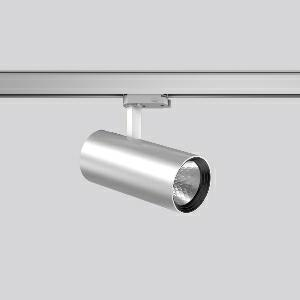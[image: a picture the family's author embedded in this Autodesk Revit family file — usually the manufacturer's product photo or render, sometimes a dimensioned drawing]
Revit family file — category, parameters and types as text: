
# Revit family: deecos_s_mini_742203_004_e2c7
name_source: partatom
category: Lighting Fixtures
units: mm (PartAtom-declared; Revit-internal decimal feet)

## family parameters
Cut with Voids When Loaded = No
Host = Face
Light Source = No
Part Type = Normal
Room Calculation Point = No
Round Connector Dimension = Use Diameter
Shared = No

## types (1)
- DEECOS S mini (1 x LED Modul 930, 3550 lm, 3000)
    Apparent Load = 29 VA
    Approval mark = CE
    CIE Flux Codes = 100 100 100 100 100
    Color Rendering = 90
    Color Temperature = 3000
    Default Elevation = 1800 mm
    Description = Series: DEECOS S mini
LED surface-mounted projector in modern design with no visible cooling ribs. Housing: die-cast aluminium, powder-coated. Rotation range: 356°. Swivel range: 90°. Black plastic ring and recessed LED to prevent glare from the side. Optical assembly with reflector made of MIRO-Silver with 98% total light reflection for outstanding efficiency - can be changed without tools. Best colour rendering index Ra>90. With multi adaptor for 3-circuit tracks 230 V. Suitable for Track on ceiling, Wall track. High quality converter without flickering and stroboscopic effect. The following accessories can be mounted without use of tools: interchangeable lenses, decorative glasses, honeycomb louvre, clear and frosted diffusers, white interchangeable plastic ring. 
Colour: silver
Diameter: 87 mm
Height: 214 mm
Lamp: LED
Socket: without socket
Colour temperature: 3000K
Colour rendering index (CRI): 92
System power: 29 W
Rated luminous flux: 3550 lm
Luminous efficiency: 122 lm/W
Control gear: Regulated power supply
Protection class: I
Type of protection: IP 20
    Height = 214 mm
    Lamp = 1 x LED Modul 930
    Lamp Light Flux = 3550 lm
    Lamp count = 1
    Length = 87 mm
    Lifetime = 50000 h
    Luminous efficacy = 122 lm/W
    Manufacturer = RZB
    ModVariant = No
    Model = 742203.004
    Mounting Place = Ceiling
    Mounting Type = Rail mounted
    Number of Poles = 1
    OnlyDefault = Yes
    Power Factor = 1
    Product Name = DEECOS S mini
    Product group = Track mounted projectors
    ProductGroupID = 301
    Protection Class = Protection class I
    Protection Degree = IP 20
    RLX_Detail_Level = 1
    RLX_Emergency_Light_Flux = 0 lm
    RLX_Emergency_Type = 0
    RLX_Emergency_Type_DB = No
    RlxData = <blob elided: 37021 chars, md5=3e0e8393>
    Socket = socket
    Standby Power = 0 W
    System Light Flux = 3550 lm
    System Power = 29 W
    Type Comments = Product without accessories
    Type Image = 741926.004.jpg
    URL = http://relux.com
    VarID = ---
    Voltage = 230 V
    Voltage Range = 220-240 V
    Weight = 0.00 kg
    Width = 0 mm  [stored 0 ft]

note: [stored X ft] marks values corroborated as IEEE doubles in the binary element streams (Revit-internal decimal feet)

## geometry (parser evidence)
native form markers: Blend x4, Sweep x11
no freeform markers — native parametric forms only
